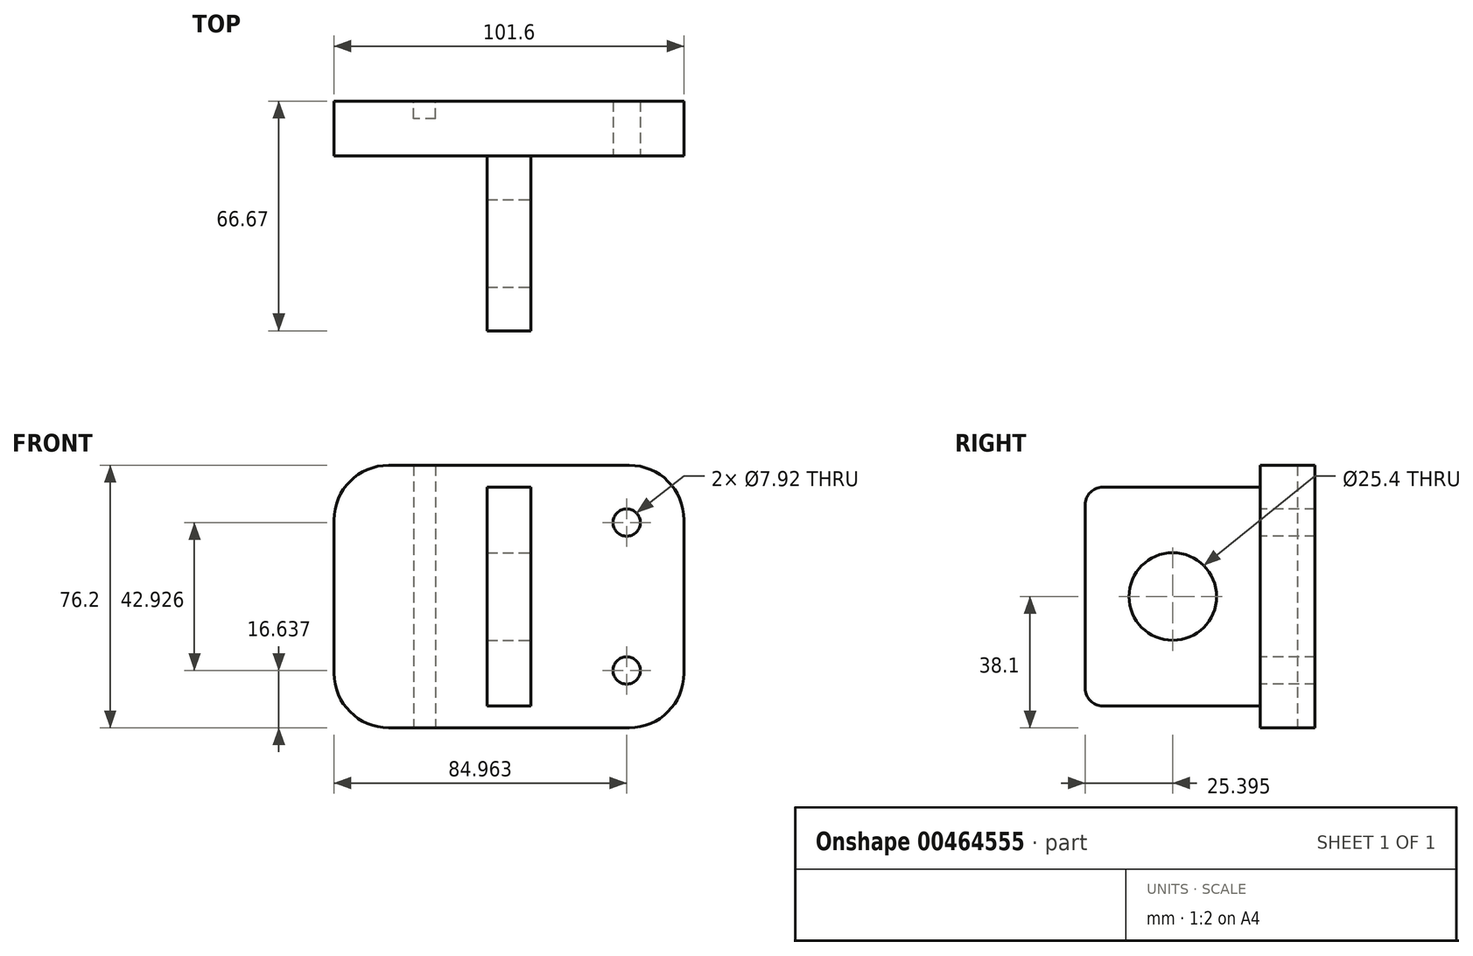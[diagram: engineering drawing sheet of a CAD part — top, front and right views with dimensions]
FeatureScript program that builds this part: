
annotation { "Feature Type Name" : "Feature", "Feature Type Description" : "" }
export const myFeature = defineFeature(function(context is Context, id is Id, definition is map)
    precondition{}
    {
        {
            var Q0;
            Q0=qCreatedBy(makeId("Front.planeOp"),FACE);
            var sketch = newSketch(context, id + "F0", { "sketchPlane" : qUnion([Q0])});
            skLineSegment(sketch, "E0.bottom", {"start": v(50.8, -38.1) * mm, "end": v(-50.8, -38.1) * mm});
            skLineSegment(sketch, "E0.top", {"start": v(50.8, 38.1) * mm, "end": v(-50.8, 38.1) * mm});
            skLineSegment(sketch, "E0.left", {"start": v(50.8, -38.1) * mm, "end": v(50.8, 38.1) * mm});
            skLineSegment(sketch, "E0.right", {"start": v(-50.8, -38.1) * mm, "end": v(-50.8, 38.1) * mm});
            skPoint(sketch, "E0.middle", {"position": v(0, 0) * mm});
            skSolve(sketch);
        }
        {
            var Q0;
            Q0=makeQuery(id+"F0.imprint","IMPRINT",FACE,{"disambiguationData":[TD([[makeQuery(id+"F0.imprint","IMPRINT",EDGE,{"derivedFrom":sQuery(id+"F0.wireOp",EDGE,"E0.bottom")}),-1.0]])]});
            extrude(context, id + "F1", {"entities" : qUnion([Q0]), "depth" : 15.88 * mm});
        }
        {
            var Q0;
            Q0=makeQuery(id+"F1.opExtrude","SWEPT_EDGE",EDGE,{"disambiguationData":[OSD([sQuery(id+"F0.wireOp",EDGE,"E0.top"),sQuery(id+"F0.wireOp",EDGE,"E0.right")])]});
            var Q1;
            Q1=makeQuery(id+"F1.opExtrude","SWEPT_EDGE",EDGE,{"disambiguationData":[OSD([sQuery(id+"F0.wireOp",EDGE,"E0.top"),sQuery(id+"F0.wireOp",EDGE,"E0.left")])]});
            var Q2;
            Q2=makeQuery(id+"F1.opExtrude","SWEPT_EDGE",EDGE,{"disambiguationData":[OSD([sQuery(id+"F0.wireOp",EDGE,"E0.bottom"),sQuery(id+"F0.wireOp",EDGE,"E0.left")])]});
            var Q3;
            Q3=makeQuery(id+"F1.opExtrude","SWEPT_EDGE",EDGE,{"disambiguationData":[OSD([sQuery(id+"F0.wireOp",EDGE,"E0.bottom"),sQuery(id+"F0.wireOp",EDGE,"E0.right")])]});
            fillet(context, id + "F2", {"entities" : qUnion([Q0, Q1, Q2, Q3]), "radius" : 15.88 * mm, "tangentPropagation" : true, "allowEdgeOverflow" : false});
        }
        {
            var Q0;
            Q0=makeQuery(id+"F1.opExtrude","CAP_FACE",FACE,{"disambiguationData":[OSD([sQuery(id+"F0.wireOp",EDGE,"E0.bottom"),sQuery(id+"F0.wireOp",EDGE,"E0.top"),sQuery(id+"F0.wireOp",EDGE,"E0.left"),sQuery(id+"F0.wireOp",EDGE,"E0.right")])],"isStart":false});
            var sketch = newSketch(context, id + "F3", { "sketchPlane" : qUnion([Q0])});
            skLineSegment(sketch, "E1", {"start": v(50.8, 38.1) * mm, "end": v(50.8, 21.46) * mm, "construction": true});
            skLineSegment(sketch, "E2", {"start": v(50.8, 21.46) * mm, "end": v(34.16, 21.46) * mm, "construction": true});
            skLineSegment(sketch, "E3", {"start": v(56.1, 23.08) * mm, "end": v(54.1, 22.73) * mm, "construction": true});
            skLineSegment(sketch, "E4", {"start": v(50.8, -38.1) * mm, "end": v(50.8, -21.46) * mm, "construction": true});
            skLineSegment(sketch, "E5", {"start": v(50.8, -21.46) * mm, "end": v(34.16, -21.46) * mm, "construction": true});
            skCircle(sketch, "E6", {"center": v(34.16, 21.46) * mm, "radius": 3.96 * mm});
            skCircle(sketch, "E7", {"center": v(34.16, -21.46) * mm, "radius": 3.96 * mm});
            skSolve(sketch);
        }
        {
            var Q0;
            Q0=makeQuery(id+"F3.imprint","IMPRINT",FACE,{"disambiguationData":[TD([[makeQuery(id+"F3.imprint","IMPRINT",EDGE,{"derivedFrom":sQuery(id+"F3.wireOp",EDGE,"E7")}),1.0]])]});
            var Q1;
            Q1=makeQuery(id+"F3.imprint","IMPRINT",FACE,{"disambiguationData":[TD([[makeQuery(id+"F3.imprint","IMPRINT",EDGE,{"derivedFrom":sQuery(id+"F3.wireOp",EDGE,"E6")}),1.0]])]});
            extrude(context, id + "F4", {"entities" : qUnion([Q0, Q1]), "operationType" : NewBodyOperationType.REMOVE, "oppositeDirection" : true, "depth" : 25.4 * mm});
        }
        {
            var Q0;
            Q0=makeQuery(id+"F1.opExtrude","CAP_FACE",FACE,{"disambiguationData":[OSD([sQuery(id+"F0.wireOp",EDGE,"E0.bottom"),sQuery(id+"F0.wireOp",EDGE,"E0.top"),sQuery(id+"F0.wireOp",EDGE,"E0.left"),sQuery(id+"F0.wireOp",EDGE,"E0.right")])],"isStart":false});
            var sketch = newSketch(context, id + "F5", { "sketchPlane" : qUnion([Q0])});
            skLineSegment(sketch, "E8.bottom", {"start": v(-6.35, 31.75) * mm, "end": v(6.35, 31.75) * mm});
            skLineSegment(sketch, "E8.top", {"start": v(-6.35, -31.75) * mm, "end": v(6.35, -31.75) * mm});
            skLineSegment(sketch, "E8.left", {"start": v(-6.35, 31.75) * mm, "end": v(-6.35, -31.75) * mm});
            skLineSegment(sketch, "E8.right", {"start": v(6.35, 31.75) * mm, "end": v(6.35, -31.75) * mm});
            skPoint(sketch, "E8.middle", {"position": v(0, 0) * mm});
            skSolve(sketch);
        }
        {
            var Q0;
            Q0=makeQuery(id+"F5.imprint","IMPRINT",FACE,{"disambiguationData":[TD([[makeQuery(id+"F5.imprint","IMPRINT",EDGE,{"derivedFrom":sQuery(id+"F5.wireOp",EDGE,"E8.bottom")}),-1.0]])]});
            extrude(context, id + "F6", {"entities" : qUnion([Q0]), "operationType" : NewBodyOperationType.ADD, "depth" : 50.8 * mm});
        }
        {
            var Q0;
            Q0=makeQuery(id+"F6.opExtrude","CAP_EDGE",EDGE,{"disambiguationData":[OSD([sQuery(id+"F5.wireOp",EDGE,"E8.top")])],"isStart":false});
            var Q1;
            Q1=makeQuery(id+"F6.opExtrude","CAP_EDGE",EDGE,{"disambiguationData":[OSD([sQuery(id+"F5.wireOp",EDGE,"E8.bottom")])],"isStart":false});
            fillet(context, id + "F7", {"entities" : qUnion([Q0, Q1]), "radius" : 5.08 * mm, "tangentPropagation" : true, "allowEdgeOverflow" : false});
        }
        {
            var Q0;
            Q0=makeQuery(id+"F6.opExtrude","SWEPT_FACE",FACE,{"disambiguationData":[OSD([sQuery(id+"F5.wireOp",EDGE,"E8.right")])]});
            var sketch = newSketch(context, id + "F8", { "sketchPlane" : qUnion([Q0])});
            skLineSegment(sketch, "E9", {"start": v(-17.9, 31.75) * mm, "end": v(-17.9, 0) * mm, "construction": true});
            skLineSegment(sketch, "E10", {"start": v(-15.88, 0) * mm, "end": v(-41.28, 0) * mm, "construction": true});
            skCircle(sketch, "E11", {"center": v(-41.28, 0) * mm, "radius": 12.7 * mm});
            skSolve(sketch);
        }
        {
            var Q0;
            Q0=makeQuery(id+"F8.imprint","IMPRINT",FACE,{"disambiguationData":[TD([[makeQuery(id+"F8.imprint","IMPRINT",EDGE,{"derivedFrom":sQuery(id+"F8.wireOp",EDGE,"E11")}),1.0]])]});
            extrude(context, id + "F9", {"entities" : qUnion([Q0]), "operationType" : NewBodyOperationType.REMOVE, "oppositeDirection" : true, "depth" : 25.4 * mm});
        }
        {
            var Q0;
            Q0=makeQuery(id+"F0.imprint","IMPRINT",FACE,{"disambiguationData":[TD([[makeQuery(id+"F0.imprint","IMPRINT",EDGE,{"derivedFrom":sQuery(id+"F0.wireOp",EDGE,"E0.bottom")}),-1.0]])]});
            var sketch = newSketch(context, id + "F10", { "sketchPlane" : qUnion([Q0])});
            skLineSegment(sketch, "E12", {"start": v(-21.32, 38.05) * mm, "end": v(-21.32, -38.2) * mm});
            skLineSegment(sketch, "E13", {"start": v(-27.67, 38.05) * mm, "end": v(-27.67, -38.2) * mm});
            skLineSegment(sketch, "E14", {"start": v(-21.32, 38.05) * mm, "end": v(-27.67, 38.05) * mm});
            skLineSegment(sketch, "E15", {"start": v(-27.67, -38.2) * mm, "end": v(-21.32, -38.2) * mm});
            skSolve(sketch);
        }
        {
            var Q0;
            {var subQ0=sQuery(id+"F10.wireOp",EDGE,"E14");Q0=makeQuery(id+"F10.imprint","IMPRINT",FACE,{"disambiguationData":[TD([[makeQuery(id+"F10.imprint","IMPRINT",EDGE,{"derivedFrom":subQ0}),1.0]])]});}
            extrude(context, id + "F11", {"entities" : qUnion([Q0]), "operationType" : NewBodyOperationType.REMOVE, "oppositeDirection" : true, "depth" : -5.08 * mm});
        }
    });
